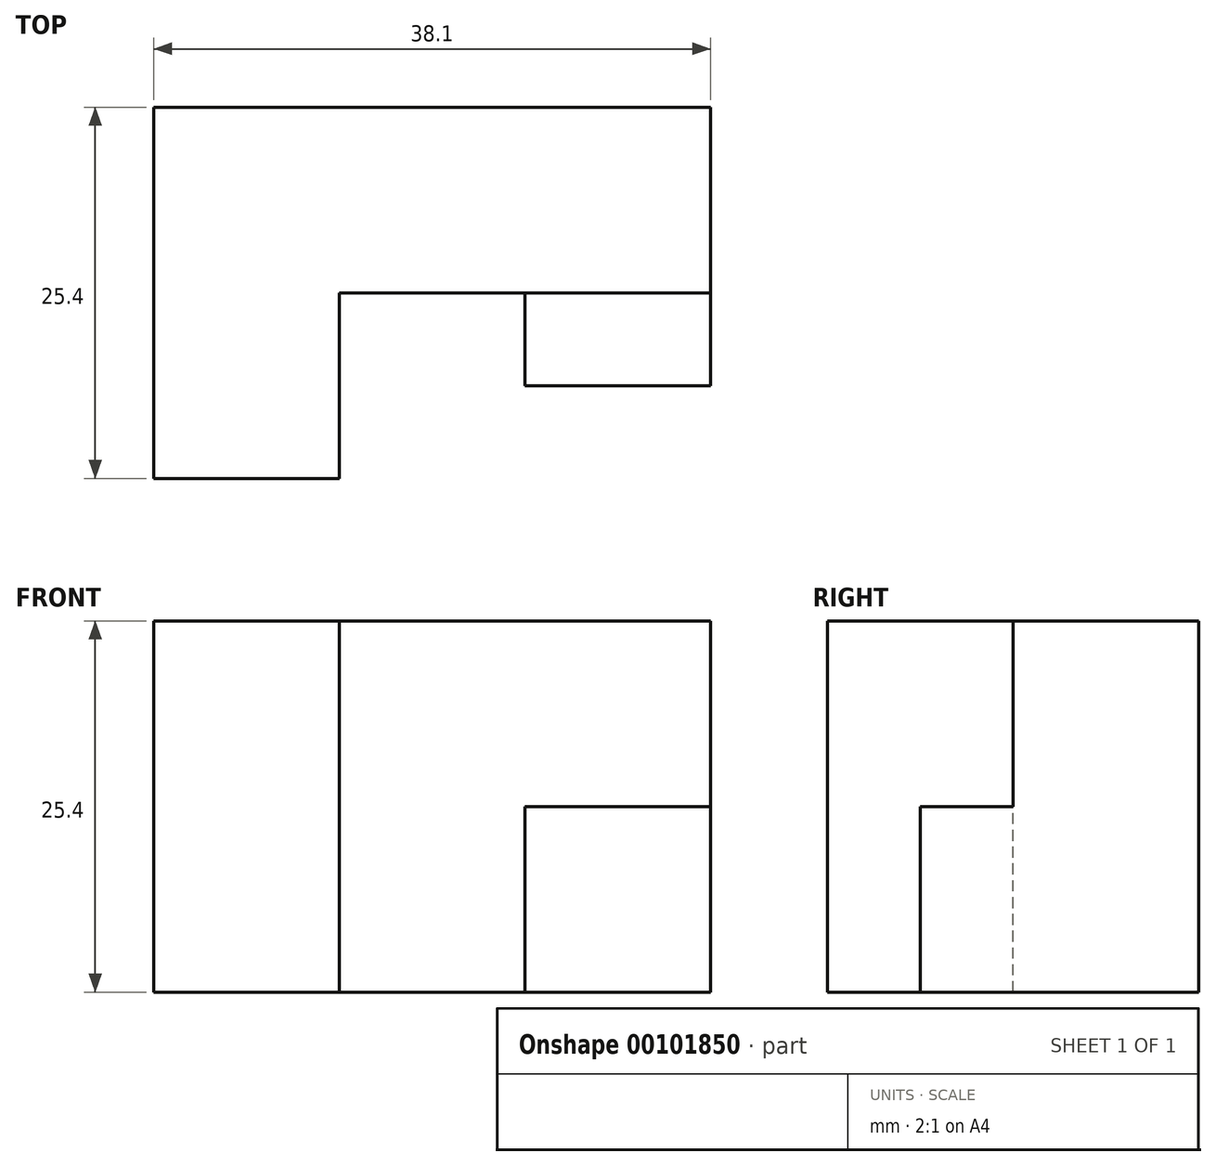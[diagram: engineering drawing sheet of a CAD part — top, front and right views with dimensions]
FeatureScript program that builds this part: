
annotation { "Feature Type Name" : "Feature", "Feature Type Description" : "" }
export const myFeature = defineFeature(function(context is Context, id is Id, definition is map)
    precondition{}
    {
        {
            var Q0;
            Q0=qCreatedBy(makeId("Top.planeOp"),FACE);
            var sketch = newSketch(context, id + "F0", { "sketchPlane" : qUnion([Q0])});
            skLineSegment(sketch, "E0", {"start": v(0, 0) * mm, "end": v(0, -25.4) * mm});
            skLineSegment(sketch, "E1", {"start": v(38.1, -25.4) * mm, "end": v(38.1, 0) * mm});
            skLineSegment(sketch, "E2", {"start": v(38.1, 0) * mm, "end": v(0, 0) * mm});
            skLineSegment(sketch, "E3", {"start": v(0, -25.4) * mm, "end": v(38.1, -25.4) * mm});
            skSolve(sketch);
        }
        {
            var Q0;
            Q0 = qSketchRegion(id + "F0", true);
            extrude(context, id + "F1", {"entities" : qUnion([Q0]), "depth" : 25.4 * mm});
        }
        {
            var Q0;
            Q0=makeQuery(id+"F1.opExtrude","CAP_FACE",FACE,{"disambiguationData":[OSD([sQuery(id+"F0.wireOp",EDGE,"E0"),sQuery(id+"F0.wireOp",EDGE,"E1"),sQuery(id+"F0.wireOp",EDGE,"E2"),sQuery(id+"F0.wireOp",EDGE,"E3")])],"isStart":false});
            var sketch = newSketch(context, id + "F2", { "sketchPlane" : qUnion([Q0])});
            skLineSegment(sketch, "E4.bottom", {"start": v(12.7, -25.4) * mm, "end": v(25.4, -25.4) * mm});
            skLineSegment(sketch, "E4.top", {"start": v(12.7, -12.7) * mm, "end": v(25.4, -12.7) * mm});
            skLineSegment(sketch, "E4.left", {"start": v(12.7, -25.4) * mm, "end": v(12.7, -12.7) * mm});
            skLineSegment(sketch, "E4.right", {"start": v(25.4, -25.4) * mm, "end": v(25.4, -12.7) * mm});
            skSolve(sketch);
        }
        {
            var Q0;
            Q0=makeQuery(id+"F2.imprint","IMPRINT",FACE,{"disambiguationData":[TD([[makeQuery(id+"F2.imprint","IMPRINT",EDGE,{"derivedFrom":sQuery(id+"F2.wireOp",EDGE,"E4.bottom")}),1.0]])]});
            extrude(context, id + "F3", {"entities" : qUnion([Q0]), "operationType" : NewBodyOperationType.REMOVE, "endBound" : BoundingType.THROUGH_ALL, "oppositeDirection" : true, "depth" : 25.4 * mm});
        }
        {
            var Q0;
            Q0=makeQuery(id+"F1.opExtrude","CAP_FACE",FACE,{"disambiguationData":[OSD([sQuery(id+"F0.wireOp",EDGE,"E0"),sQuery(id+"F0.wireOp",EDGE,"E1"),sQuery(id+"F0.wireOp",EDGE,"E2"),sQuery(id+"F0.wireOp",EDGE,"E3")])],"isStart":false});
            var sketch = newSketch(context, id + "F4", { "sketchPlane" : qUnion([Q0])});
            skLineSegment(sketch, "E5.bottom", {"start": v(38.1, -25.4) * mm, "end": v(25.4, -25.4) * mm});
            skLineSegment(sketch, "E5.top", {"start": v(38.1, -19.05) * mm, "end": v(25.4, -19.05) * mm});
            skLineSegment(sketch, "E5.left", {"start": v(38.1, -25.4) * mm, "end": v(38.1, -19.05) * mm});
            skLineSegment(sketch, "E5.right", {"start": v(25.4, -25.4) * mm, "end": v(25.4, -19.05) * mm});
            skSolve(sketch);
        }
        {
            var Q0;
            Q0 = qSketchRegion(id + "F4", true);
            extrude(context, id + "F5", {"entities" : qUnion([Q0]), "operationType" : NewBodyOperationType.REMOVE, "endBound" : BoundingType.THROUGH_ALL, "oppositeDirection" : true, "depth" : 25.4 * mm});
        }
        {
            var Q0;
            Q0=makeQuery(id+"F1.opExtrude","CAP_FACE",FACE,{"disambiguationData":[OSD([sQuery(id+"F0.wireOp",EDGE,"E0"),sQuery(id+"F0.wireOp",EDGE,"E1"),sQuery(id+"F0.wireOp",EDGE,"E2"),sQuery(id+"F0.wireOp",EDGE,"E3")])],"isStart":false});
            var sketch = newSketch(context, id + "F6", { "sketchPlane" : qUnion([Q0])});
            skLineSegment(sketch, "E6.bottom", {"start": v(25.4, -19.05) * mm, "end": v(38.1, -19.05) * mm});
            skLineSegment(sketch, "E6.top", {"start": v(25.4, -12.7) * mm, "end": v(38.1, -12.7) * mm});
            skLineSegment(sketch, "E6.left", {"start": v(25.4, -19.05) * mm, "end": v(25.4, -12.7) * mm});
            skLineSegment(sketch, "E6.right", {"start": v(38.1, -19.05) * mm, "end": v(38.1, -12.7) * mm});
            skSolve(sketch);
        }
        {
            var Q0;
            Q0 = qSketchRegion(id + "F6", true);
            extrude(context, id + "F7", {"entities" : qUnion([Q0]), "operationType" : NewBodyOperationType.REMOVE, "oppositeDirection" : true, "depth" : 12.7 * mm});
        }
    });
